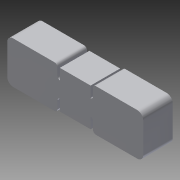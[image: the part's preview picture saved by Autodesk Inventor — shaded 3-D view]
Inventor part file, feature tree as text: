
AUTODESK INVENTOR PART (.ipt)
format: ipt  version: 2015 (Build 190159000, 159)  size: 111,104 bytes
history: native  units: in
note: dims shown in document units (in); Inventor stores cm internally (conversion verified against a paired STEP export)
features: extrude x1, sketch x1
ambient origin geometry x8: Origin, YZ Plane, XZ Plane, XY Plane, X Axis, Y Axis, Z Axis, Center Point
bodies: Solid1 (feature_tree)
feature tree (2):
  extrude  "Extrusion1"  Depth=0.5in
  sketch  "Sketch1"  dims[d0=0.32in d2=1.15in d4=0.04in d5=0.04in d10=0.05in d11=0.1in d12=0.22in d13=0.5in d14=0.0in]
